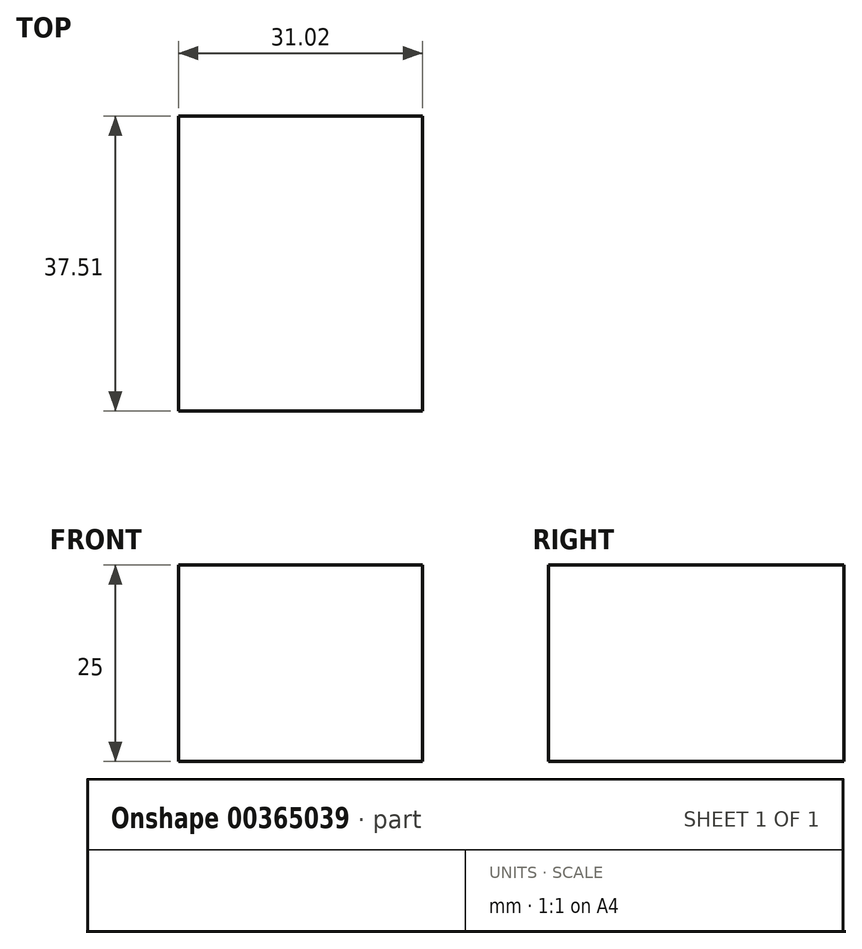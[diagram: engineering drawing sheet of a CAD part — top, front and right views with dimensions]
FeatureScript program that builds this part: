
annotation { "Feature Type Name" : "Feature", "Feature Type Description" : "" }
export const myFeature = defineFeature(function(context is Context, id is Id, definition is map)
    precondition{}
    {
        {
            var Q0;
            Q0=qCreatedBy(makeId("Top.planeOp"),FACE);
            var sketch = newSketch(context, id + "F0", { "sketchPlane" : qUnion([Q0])});
            skLineSegment(sketch, "E0.bottom", {"start": v(-59.65, -19.74) * mm, "end": v(-28.63, -19.74) * mm});
            skLineSegment(sketch, "E0.top", {"start": v(-59.65, 17.77) * mm, "end": v(-28.63, 17.77) * mm});
            skLineSegment(sketch, "E0.left", {"start": v(-59.65, -19.74) * mm, "end": v(-59.65, 17.77) * mm});
            skLineSegment(sketch, "E0.right", {"start": v(-28.63, -19.74) * mm, "end": v(-28.63, 17.77) * mm});
            skSolve(sketch);
        }
        {
            var Q0;
            Q0 = qSketchRegion(id + "F0", true);
            extrude(context, id + "F1", {"entities" : qUnion([Q0]), "depth" : 25 * mm});
        }
    });
